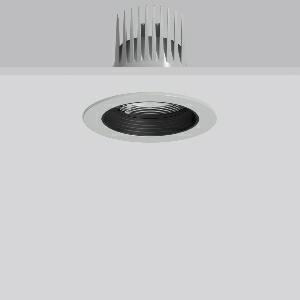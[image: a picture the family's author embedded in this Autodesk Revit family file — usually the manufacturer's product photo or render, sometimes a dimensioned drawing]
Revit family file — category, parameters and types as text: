
# Revit family: heledon_maxi_e_901761_004_1_0032
name_source: partatom
category: Lighting Fixtures
units: mm (PartAtom-declared; Revit-internal decimal feet)

## family parameters
Cut with Voids When Loaded = No
Host = Face
Light Source = No
Part Type = Normal
Room Calculation Point = No
Round Connector Dimension = Use Diameter
Shared = No

## types (1)
- HELEDON maxi E (1 x LED Modul 940, 2850 lm, 4000)
    Apparent Load = 25 VA
    Approval mark = CE
    CIE Flux Codes = 96 100 100 100 100
    Color Rendering = 92
    Color Temperature = 4000
    Default Elevation = 1800 mm
    Description = Series: HELEDON maxi
Round recessed downlight. Housing: die-cast aluminium, powder-coated. Black plastic ring and recessed LED to prevent glare from the side. Optical assembly with lens made of plastic (polycarbonate) for the best homogeneous light distribution - can be changed without tools. Best colour rendering index Ra>90. Suitable for Recessed ceiling mounting. Installation without tools thanks to spring fastening system. Including separate LED converter with connecting cable 600 mm.High quality converter without flickering and stroboscopic effect. Through-wiring box (5 pole) available as accessory. The following accessories can be mounted without use of tools: interchangeable lenses, decorative glasses, honeycomb louvre, clear and frosted diffusers, white interchangeable plastic ring. 
Colour: silver
Diameter: 162 mm
Height: 3 mm
Cut-out diameter: 152 mm
Recess height: 200 mm
Luminaire: recess height: 135 mm
Lamp: LED
Socket: without socket
Colour temperature: 4000K
Colour rendering index (CRI): 92
System power: 25 W
Rated luminous flux: 2850 lm
Luminous efficiency: 114 lm/W
Control gear: Regulated power supply
Protection class: II
Type of protection: IP 20
    Height = 0 mm  [stored 0 ft]
    Lamp = 1 x LED Modul 940
    Lamp Light Flux = 2850 lm
    Lamp count = 1
    Length = 162 mm
    Lifetime = 50000 h
    Luminous efficacy = 114 lm/W
    Manufacturer = RZB
    ModVariant = No
    Model = 901761.004.1
    Mounting Place = Ceiling
    Mounting Type = Recessed
    Number of Poles = 1
    OnlyDefault = Yes
    Power Factor = 1
    Product Name = HELEDON maxi E
    Product group = Recessed downlights
    ProductGroupID = 402
    Protection Class = Protection class II
    Protection Degree = IP 20
    RLX_Detail_Level = 1
    RLX_Emergency_Light_Flux = 0 lm
    RLX_Emergency_Type = 0
    RLX_Emergency_Type_DB = No
    RlxData = <blob elided: 120037 chars, md5=dbabedc1>
    Socket = socket
    Standby Power = 0 W
    System Light Flux = 2850 lm
    System Power = 25 W
    Type Comments = Product without accessories
    Type Image = 901663.004.jpg
    URL = http://relux.com
    VarID = ---
    Voltage = 230 V
    Voltage Range = 220-240 V
    Weight = 0.00 kg
    Width = 0 mm  [stored 0 ft]

note: [stored X ft] marks values corroborated as IEEE doubles in the binary element streams (Revit-internal decimal feet)

## geometry (parser evidence)
native form markers: Blend x4, Sweep x11
no freeform markers — native parametric forms only
